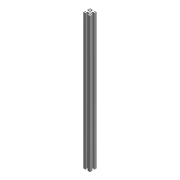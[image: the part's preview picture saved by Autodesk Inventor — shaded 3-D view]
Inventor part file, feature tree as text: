
AUTODESK INVENTOR PART (.ipt)
format: ipt  version: 2019 (Build 230136000, 136)  size: 151,040 bytes
history: native  units: mm
features: other x4, extrude x1, sketch x1, reference x1
ambient origin geometry x8: Origin, YZ Plane, XZ Plane, XY Plane, X Axis, Y Axis, Z Axis, Center Point
bodies: Body1 (feature_tree)
feature tree (7):
  other  "솔리드1"
  extrude  "돌출1"  Depth=400.0mm TaperAngle=0.0deg
  sketch  "스케치1"
  reference  "참조1"
  other  "<userpath>\Documents\Inventor\Projects\2019_CapstoneDesign\Body.iam"
  other  "Body.iam"
  other  "Propile_202070:4"
